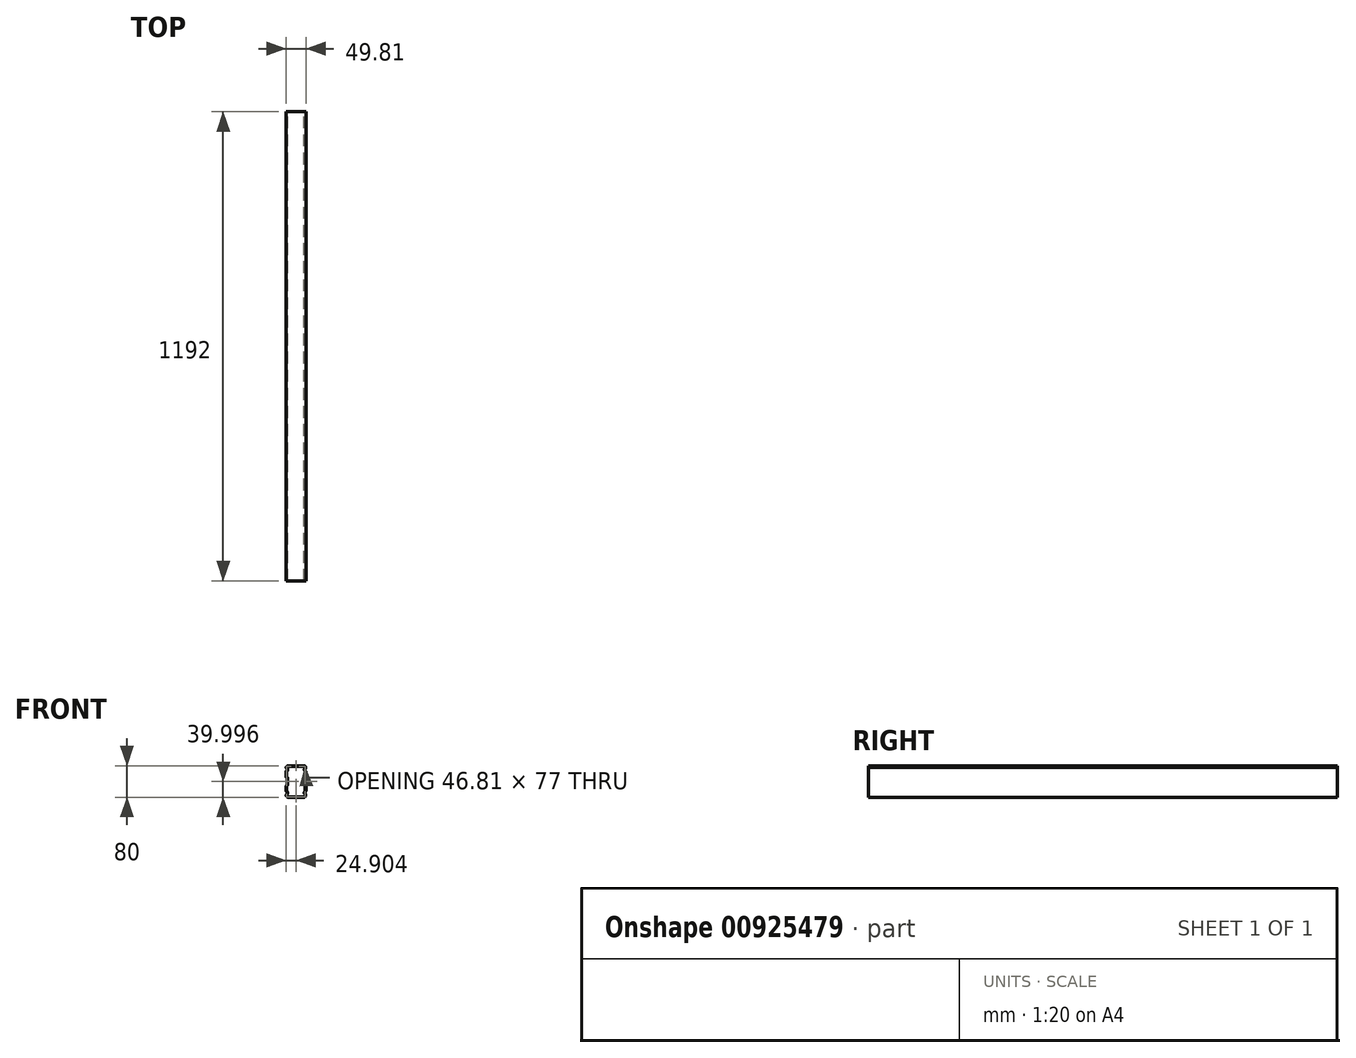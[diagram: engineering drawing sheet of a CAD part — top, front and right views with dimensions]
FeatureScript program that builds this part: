
annotation { "Feature Type Name" : "Feature", "Feature Type Description" : "" }
export const myFeature = defineFeature(function(context is Context, id is Id, definition is map)
    precondition{}
    {
        {
            var Q0;
            Q0=qCreatedBy(makeId("Front.planeOp"),FACE);
            var sketch = newSketch(context, id + "F0", { "sketchPlane" : qUnion([Q0])});
            skLineSegment(sketch, "E0.bottom", {"start": v(-66.37, 65.7) * mm, "end": v(-26.18, 65.7) * mm});
            skLineSegment(sketch, "E0.top", {"start": v(-66.18, -14.3) * mm, "end": v(-26.18, -14.3) * mm});
            skArc(sketch, "E1.filletArc", {"start": v(-66.37, 65.7) * mm, "mid": v(-69.38, 64.7) * mm, "end": v(-71.18, 62.07) * mm});
            skArc(sketch, "E2.filletArc", {"start": v(-71.18, -9.3) * mm, "mid": v(-69.72, -12.83) * mm, "end": v(-66.18, -14.3) * mm});
            skArc(sketch, "E3", {"start": v(-69.34, -4.86) * mm, "mid": v(-70.7, -6.9) * mm, "end": v(-71.18, -9.3) * mm});
            skArc(sketch, "E4", {"start": v(-68.78, -3.08) * mm, "mid": v(-69.4, -1.3) * mm, "end": v(-70.56, 0.2) * mm});
            skArc(sketch, "E5.filletArc", {"start": v(-69.34, -4.86) * mm, "mid": v(-68.84, -4.04) * mm, "end": v(-68.78, -3.08) * mm});
            skLineSegment(sketch, "E6", {"start": v(-71.18, 1.64) * mm, "end": v(-71.18, 14.24) * mm});
            skLineSegment(sketch, "E7", {"start": v(-71.18, 15.7) * mm, "end": v(-71.18, 15.7) * mm});
            skLineSegment(sketch, "E8", {"start": v(-69.18, 17.7) * mm, "end": v(-69.18, 33.7) * mm});
            skLineSegment(sketch, "E9", {"start": v(-71.18, 35.7) * mm, "end": v(-71.18, 35.7) * mm});
            skArc(sketch, "E10.filletArc", {"start": v(-70.18, 15.97) * mm, "mid": v(-69.45, 16.7) * mm, "end": v(-69.18, 17.7) * mm});
            skPoint(sketch, "E11.visualSharp", {"position": v(-71.18, 15.7) * mm});
            skArc(sketch, "E11.filletArc", {"start": v(-70.18, 15.97) * mm, "mid": v(-70.91, 15.24) * mm, "end": v(-71.18, 14.24) * mm});
            skArc(sketch, "E12.filletArc", {"start": v(-69.18, 33.7) * mm, "mid": v(-69.45, 34.7) * mm, "end": v(-70.18, 35.44) * mm});
            skPoint(sketch, "E13.visualSharp", {"position": v(-71.18, 35.7) * mm});
            skArc(sketch, "E13.filletArc", {"start": v(-71.18, 37.17) * mm, "mid": v(-70.91, 36.17) * mm, "end": v(-70.18, 35.44) * mm});
            skArc(sketch, "E14.filletArc", {"start": v(-71.18, 1.64) * mm, "mid": v(-71.02, 0.85) * mm, "end": v(-70.56, 0.2) * mm});
            skArc(sketch, "E15", {"start": v(-71.18, 62.07) * mm, "mid": v(-70.7, 59.68) * mm, "end": v(-69.35, 57.65) * mm});
            skArc(sketch, "E16", {"start": v(-70.57, 52.6) * mm, "mid": v(-69.44, 54.09) * mm, "end": v(-68.8, 55.85) * mm});
            skArc(sketch, "E17.filletArc", {"start": v(-68.8, 55.85) * mm, "mid": v(-68.85, 56.82) * mm, "end": v(-69.35, 57.65) * mm});
            skArc(sketch, "E18.filletArc", {"start": v(-70.57, 52.6) * mm, "mid": v(-71.02, 51.94) * mm, "end": v(-71.18, 51.16) * mm});
            skLineSegment(sketch, "E19", {"start": v(-71.18, 37.17) * mm, "end": v(-71.18, 51.16) * mm});
            skArc(sketch, "E20.MirrorCS", {"start": v(-21.37, 37.17) * mm, "mid": v(-21.64, 36.17) * mm, "end": v(-22.37, 35.44) * mm});
            skArc(sketch, "E21.MirrorCS", {"start": v(-23.37, 33.7) * mm, "mid": v(-23.1, 34.7) * mm, "end": v(-22.37, 35.44) * mm});
            skArc(sketch, "E22.MirrorCS", {"start": v(-22.37, 15.97) * mm, "mid": v(-23.1, 16.7) * mm, "end": v(-23.37, 17.7) * mm});
            skArc(sketch, "E23.MirrorCS", {"start": v(-22.37, 15.97) * mm, "mid": v(-21.64, 15.24) * mm, "end": v(-21.37, 14.24) * mm});
            skArc(sketch, "E24.MirrorCS", {"start": v(-21.98, 52.6) * mm, "mid": v(-21.53, 51.94) * mm, "end": v(-21.37, 51.16) * mm});
            skArc(sketch, "E25.MirrorCS", {"start": v(-23.22, -4.86) * mm, "mid": v(-23.71, -4.04) * mm, "end": v(-23.77, -3.08) * mm});
            skArc(sketch, "E26.MirrorCS", {"start": v(-21.37, 1.64) * mm, "mid": v(-21.53, 0.85) * mm, "end": v(-22, 0.2) * mm});
            skArc(sketch, "E27.MirrorCS", {"start": v(-23.75, 55.85) * mm, "mid": v(-23.7, 56.82) * mm, "end": v(-23.2, 57.65) * mm});
            skArc(sketch, "E28.MirrorCS", {"start": v(-21.98, 52.6) * mm, "mid": v(-23.11, 54.09) * mm, "end": v(-23.75, 55.85) * mm});
            skArc(sketch, "E29.MirrorCS", {"start": v(-23.77, -3.08) * mm, "mid": v(-23.14, -1.3) * mm, "end": v(-22, 0.2) * mm});
            skArc(sketch, "E30.MirrorCS", {"start": v(-21.37, 62.07) * mm, "mid": v(-21.85, 59.68) * mm, "end": v(-23.2, 57.65) * mm});
            skArc(sketch, "E31.MirrorCS", {"start": v(-23.22, -4.86) * mm, "mid": v(-21.85, -6.9) * mm, "end": v(-21.37, -9.3) * mm});
            skPoint(sketch, "E32.MirrorP", {"position": v(-21.37, 35.7) * mm});
            skArc(sketch, "E33.MirrorCS", {"start": v(-21.37, -9.3) * mm, "mid": v(-22.84, -12.83) * mm, "end": v(-26.37, -14.3) * mm});
            skArc(sketch, "E34.MirrorCS", {"start": v(-26.18, 65.7) * mm, "mid": v(-23.17, 64.7) * mm, "end": v(-21.37, 62.07) * mm});
            skPoint(sketch, "E35.MirrorP", {"position": v(-21.37, 52.07) * mm});
            skPoint(sketch, "E36.MirrorP", {"position": v(-23.37, 35.7) * mm});
            skLineSegment(sketch, "E37.MirrorCS", {"start": v(-21.37, 37.17) * mm, "end": v(-21.37, 51.16) * mm});
            skPoint(sketch, "E38.MirrorP", {"position": v(-23.87, 57.07) * mm});
            skLineSegment(sketch, "E39.MirrorCS", {"start": v(-21.37, 1.64) * mm, "end": v(-21.37, 14.24) * mm});
            skLineSegment(sketch, "E40.MirrorCS", {"start": v(-23.37, 17.7) * mm, "end": v(-23.37, 33.7) * mm});
            skSolve(sketch);
        }
        {
            var Q0;
            Q0=makeQuery(id+"F0.imprint","IMPRINT",FACE,{"disambiguationData":[TD([[makeQuery(id+"F0.imprint","IMPRINT",EDGE,{"derivedFrom":sQuery(id+"F0.wireOp",EDGE,"E0.bottom")}),-1.0]])]});
            extrude(context, id + "F1", {"entities" : qUnion([Q0]), "depth" : 1192 * mm, "offsetDistance" : 25 * mm});
        }
        {
            var Q0;
            Q0=makeQuery(id+"F1.opExtrude","CAP_FACE",FACE,{"disambiguationData":[OSD([sQuery(id+"F0.wireOp",EDGE,"E0.bottom"),sQuery(id+"F0.wireOp",EDGE,"E0.top"),sQuery(id+"F0.wireOp",EDGE,"E1.filletArc"),sQuery(id+"F0.wireOp",EDGE,"E2.filletArc"),sQuery(id+"F0.wireOp",EDGE,"E3"),sQuery(id+"F0.wireOp",EDGE,"E4"),sQuery(id+"F0.wireOp",EDGE,"E5.filletArc"),sQuery(id+"F0.wireOp",EDGE,"E6"),sQuery(id+"F0.wireOp",EDGE,"E8"),sQuery(id+"F0.wireOp",EDGE,"E10.filletArc"),sQuery(id+"F0.wireOp",EDGE,"E11.filletArc"),sQuery(id+"F0.wireOp",EDGE,"E12.filletArc"),sQuery(id+"F0.wireOp",EDGE,"E13.filletArc"),sQuery(id+"F0.wireOp",EDGE,"E14.filletArc"),sQuery(id+"F0.wireOp",EDGE,"E15"),sQuery(id+"F0.wireOp",EDGE,"E16"),sQuery(id+"F0.wireOp",EDGE,"E17.filletArc"),sQuery(id+"F0.wireOp",EDGE,"E18.filletArc"),sQuery(id+"F0.wireOp",EDGE,"E19"),sQuery(id+"F0.wireOp",EDGE,"E20.MirrorCS"),sQuery(id+"F0.wireOp",EDGE,"E21.MirrorCS"),sQuery(id+"F0.wireOp",EDGE,"E22.MirrorCS"),sQuery(id+"F0.wireOp",EDGE,"E23.MirrorCS"),sQuery(id+"F0.wireOp",EDGE,"E24.MirrorCS"),sQuery(id+"F0.wireOp",EDGE,"E25.MirrorCS"),sQuery(id+"F0.wireOp",EDGE,"E26.MirrorCS"),sQuery(id+"F0.wireOp",EDGE,"E27.MirrorCS"),sQuery(id+"F0.wireOp",EDGE,"E28.MirrorCS"),sQuery(id+"F0.wireOp",EDGE,"E29.MirrorCS"),sQuery(id+"F0.wireOp",EDGE,"E30.MirrorCS"),sQuery(id+"F0.wireOp",EDGE,"E31.MirrorCS"),sQuery(id+"F0.wireOp",EDGE,"E33.MirrorCS"),sQuery(id+"F0.wireOp",EDGE,"E34.MirrorCS"),sQuery(id+"F0.wireOp",EDGE,"E37.MirrorCS"),sQuery(id+"F0.wireOp",EDGE,"E39.MirrorCS"),sQuery(id+"F0.wireOp",EDGE,"E40.MirrorCS")])],"isStart":false});
            var Q1;
            Q1=makeQuery(id+"F1.opExtrude","CAP_FACE",FACE,{"disambiguationData":[OSD([sQuery(id+"F0.wireOp",EDGE,"E0.bottom"),sQuery(id+"F0.wireOp",EDGE,"E0.top"),sQuery(id+"F0.wireOp",EDGE,"E1.filletArc"),sQuery(id+"F0.wireOp",EDGE,"E2.filletArc"),sQuery(id+"F0.wireOp",EDGE,"E3"),sQuery(id+"F0.wireOp",EDGE,"E4"),sQuery(id+"F0.wireOp",EDGE,"E5.filletArc"),sQuery(id+"F0.wireOp",EDGE,"E6"),sQuery(id+"F0.wireOp",EDGE,"E8"),sQuery(id+"F0.wireOp",EDGE,"E10.filletArc"),sQuery(id+"F0.wireOp",EDGE,"E11.filletArc"),sQuery(id+"F0.wireOp",EDGE,"E12.filletArc"),sQuery(id+"F0.wireOp",EDGE,"E13.filletArc"),sQuery(id+"F0.wireOp",EDGE,"E14.filletArc"),sQuery(id+"F0.wireOp",EDGE,"E15"),sQuery(id+"F0.wireOp",EDGE,"E16"),sQuery(id+"F0.wireOp",EDGE,"E17.filletArc"),sQuery(id+"F0.wireOp",EDGE,"E18.filletArc"),sQuery(id+"F0.wireOp",EDGE,"E19"),sQuery(id+"F0.wireOp",EDGE,"E20.MirrorCS"),sQuery(id+"F0.wireOp",EDGE,"E21.MirrorCS"),sQuery(id+"F0.wireOp",EDGE,"E22.MirrorCS"),sQuery(id+"F0.wireOp",EDGE,"E23.MirrorCS"),sQuery(id+"F0.wireOp",EDGE,"E24.MirrorCS"),sQuery(id+"F0.wireOp",EDGE,"E25.MirrorCS"),sQuery(id+"F0.wireOp",EDGE,"E26.MirrorCS"),sQuery(id+"F0.wireOp",EDGE,"E27.MirrorCS"),sQuery(id+"F0.wireOp",EDGE,"E28.MirrorCS"),sQuery(id+"F0.wireOp",EDGE,"E29.MirrorCS"),sQuery(id+"F0.wireOp",EDGE,"E30.MirrorCS"),sQuery(id+"F0.wireOp",EDGE,"E31.MirrorCS"),sQuery(id+"F0.wireOp",EDGE,"E33.MirrorCS"),sQuery(id+"F0.wireOp",EDGE,"E34.MirrorCS"),sQuery(id+"F0.wireOp",EDGE,"E37.MirrorCS"),sQuery(id+"F0.wireOp",EDGE,"E39.MirrorCS"),sQuery(id+"F0.wireOp",EDGE,"E40.MirrorCS")])],"isStart":true});
            shell(context, id + "F2", {"entities" : qUnion([Q0, Q1]), "thickness" : 1.5 * mm});
        }
    });
